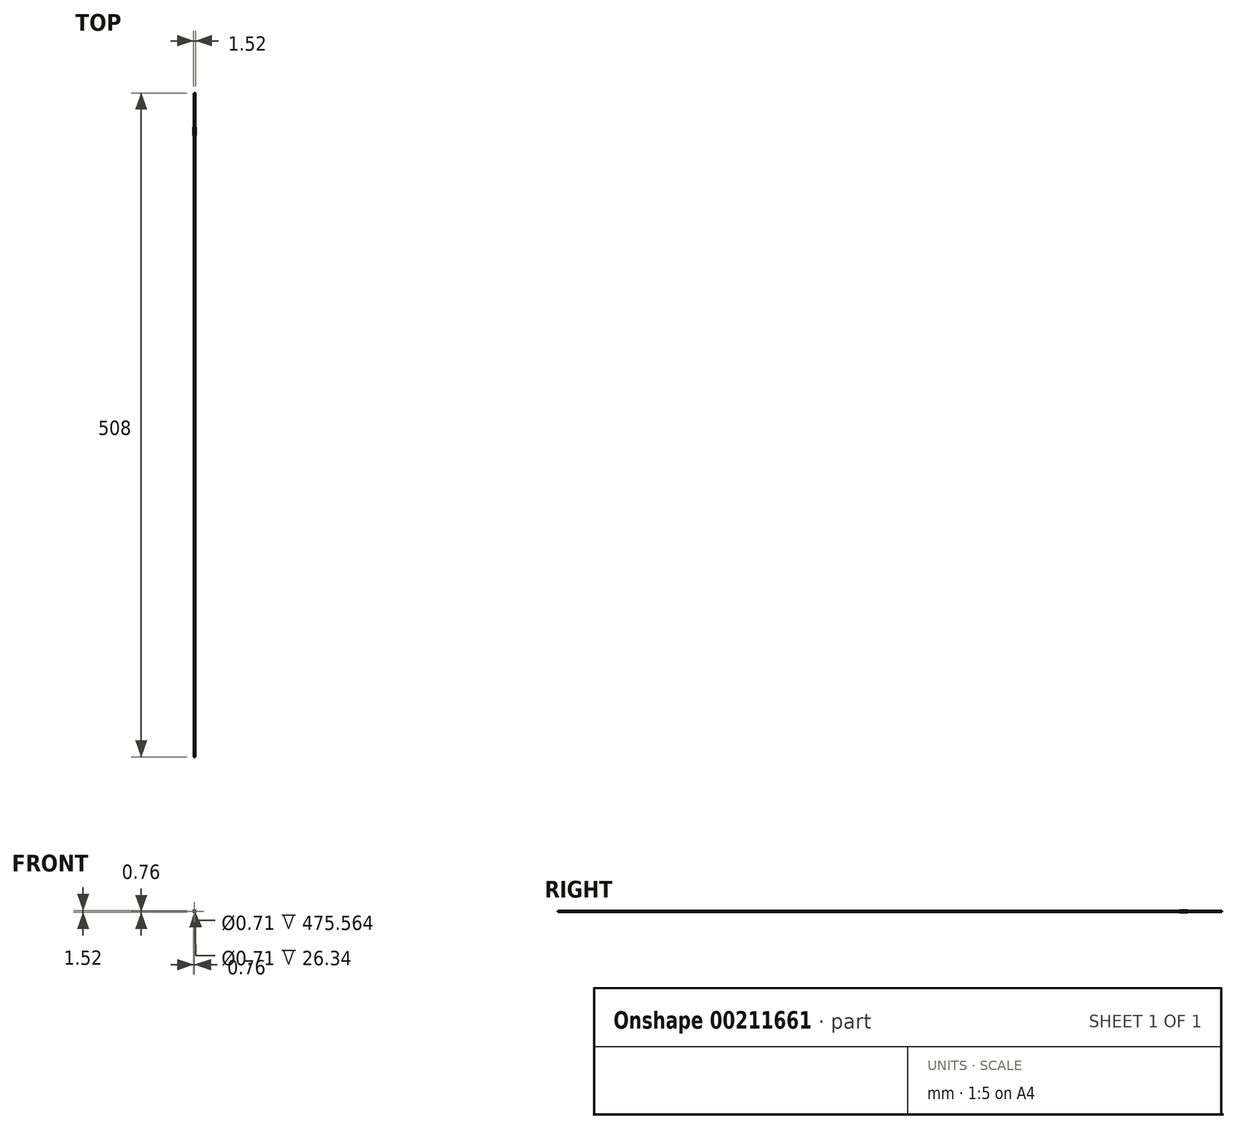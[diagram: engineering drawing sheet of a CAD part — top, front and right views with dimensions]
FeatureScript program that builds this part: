
annotation { "Feature Type Name" : "Feature", "Feature Type Description" : "" }
export const myFeature = defineFeature(function(context is Context, id is Id, definition is map)
    precondition{}
    {
        {
            var Q0;
            Q0=qCreatedBy(makeId("Front.planeOp"),FACE);
            var sketch = newSketch(context, id + "F0", { "sketchPlane" : qUnion([Q0])});
            skCircle(sketch, "E0", {"center": v(0, 0) * mm, "radius": 0.36 * mm});
            skCircle(sketch, "E1", {"center": v(0, 0) * mm, "radius": 0.43 * mm});
            skSolve(sketch);
        }
        {
            var Q0;
            Q0=qSketchRegion(id+"F0",true);
            extrude(context, id + "F1", {"entities" : qUnion([Q0]), "depth" : 508 * mm});
        }
        {
            var Q0;
            Q0=qCreatedBy(makeId("Front.planeOp"),FACE);
            cPlane(context, id + "F2", {"entities" : qUnion([Q0]), "cplaneType" : CPlaneType.OFFSET, "offset" : 26.34 * mm, "width" : 152.4 * mm, "height" : 152.4 * mm});
        }
        {
            var Q0;
            Q0=qCreatedBy(id+"F2.planeOp",FACE);
            var sketch = newSketch(context, id + "F3", { "sketchPlane" : qUnion([Q0])});
            skCircle(sketch, "E2", {"center": v(0, 0) * mm, "radius": 0.76 * mm});
            skSolve(sketch);
        }
        {
            var Q0;
            Q0=qSketchRegion(id+"F3",true);
            extrude(context, id + "F4", {"entities" : qUnion([Q0]), "operationType" : NewBodyOperationType.ADD, "depth" : 6.1 * mm});
        }
    });
